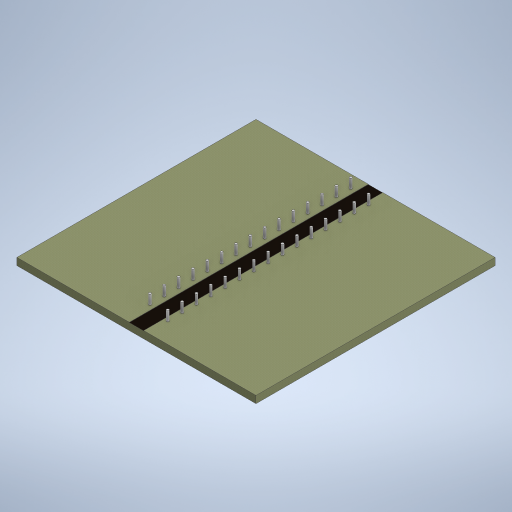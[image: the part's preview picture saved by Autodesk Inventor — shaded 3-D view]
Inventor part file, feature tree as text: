
AUTODESK INVENTOR PART (.ipt)
format: ipt  version: 2023 (Build 270158000, 158)  size: 316,416 bytes
history: native  units: in
note: dims shown in document units (in); Inventor stores cm internally (conversion verified against a paired STEP export)
features: extrude x3, sketch x3, pattern_linear x2, projected_geometry x1
ambient origin geometry x8: Origin, YZ Plane, XZ Plane, XY Plane, X Axis, Y Axis, Z Axis, Center Point
bodies: Solid1 (feature_tree)
feature tree (9):
  extrude  "Extrusion1"  Depth=3937.0079in
  extrude  "Extrusion2"  Depth=236.2205in
  extrude  "Extrusion3"  Depth=236.2205in
  pattern_linear  "Rectangular Pattern1"  Count1=100 Spacing1=0.0in
  pattern_linear  "Rectangular Pattern2"  Count1=8  [1 undecoded]
  sketch  "Sketch1"  dims[d0=3937.0079in d1=3937.0079in]
  sketch  "Sketch2"  dims[d2=118.1102in d3=0.0in d4=236.2205in]
  sketch  "Sketch3"  dims[d5=3.937in d6=0.0in d7=39.3701in d8=39.3701in d9=157.4803in d10=0.0in d11=3.1496in d13=236.2205in d14=3.1496in d16=236.2205in]
  projected_geometry  "Projected Loop1"
note: 1 required parameter value undecoded (feature->parameter linkage not recoverable at this tier; creation-order binding heuristic only, values carry confidence <= 0.55)
